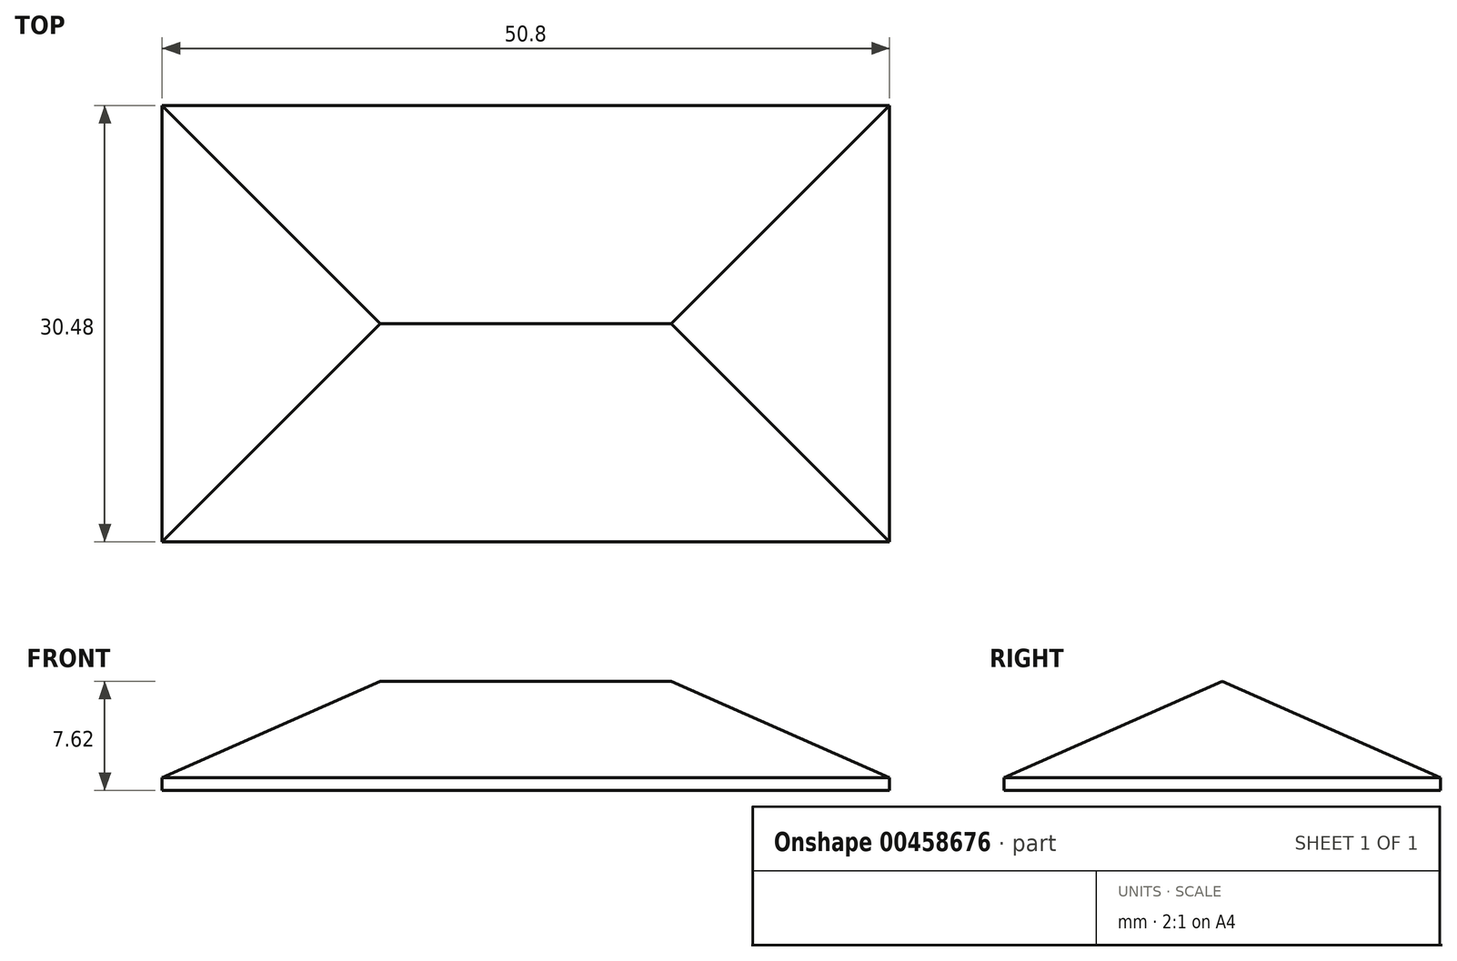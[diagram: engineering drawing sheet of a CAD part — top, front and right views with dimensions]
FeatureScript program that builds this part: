
annotation { "Feature Type Name" : "Feature", "Feature Type Description" : "" }
export const myFeature = defineFeature(function(context is Context, id is Id, definition is map)
    precondition{}
    {
        {
            var Q0;
            Q0=qCreatedBy(makeId("Top.planeOp"),FACE);
            var sketch = newSketch(context, id + "F0", { "sketchPlane" : qUnion([Q0])});
            skLineSegment(sketch, "E0.bottom", {"start": v(25.4, 15.24) * mm, "end": v(-25.4, 15.24) * mm});
            skLineSegment(sketch, "E0.top", {"start": v(25.4, -15.24) * mm, "end": v(-25.4, -15.24) * mm});
            skLineSegment(sketch, "E0.left", {"start": v(25.4, 15.24) * mm, "end": v(25.4, -15.24) * mm});
            skLineSegment(sketch, "E0.right", {"start": v(-25.4, 15.24) * mm, "end": v(-25.4, -15.24) * mm});
            skPoint(sketch, "E0.middle", {"position": v(0, 0) * mm});
            skSolve(sketch);
        }
        {
            var Q0;
            Q0 = qSketchRegion(id + "F0", true);
            extrude(context, id + "F1", {"entities" : qUnion([Q0]), "depth" : 7.62 * mm});
        }
        {
            var Q0;
            Q0=makeQuery(id+"F1.opExtrude","CAP_EDGE",EDGE,{"disambiguationData":[OSD([sQuery(id+"F0.wireOp",EDGE,"E0.right")])],"isStart":false});
            var Q1;
            Q1=makeQuery(id+"F1.opExtrude","CAP_EDGE",EDGE,{"disambiguationData":[OSD([sQuery(id+"F0.wireOp",EDGE,"E0.bottom")])],"isStart":false});
            var Q2;
            Q2=makeQuery(id+"F1.opExtrude","CAP_EDGE",EDGE,{"disambiguationData":[OSD([sQuery(id+"F0.wireOp",EDGE,"E0.top")])],"isStart":false});
            var Q3;
            Q3=makeQuery(id+"F1.opExtrude","CAP_EDGE",EDGE,{"disambiguationData":[OSD([sQuery(id+"F0.wireOp",EDGE,"E0.left")])],"isStart":false});
            chamfer(context, id + "F2", {"entities" : qUnion([Q0, Q1, Q2, Q3]), "chamferType" : ChamferType.TWO_OFFSETS, "width1" : 15.24 * mm, "oppositeDirection" : false, "width2" : 6.73 * mm, "tangentPropagation" : true});
        }
    });
